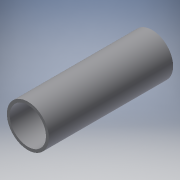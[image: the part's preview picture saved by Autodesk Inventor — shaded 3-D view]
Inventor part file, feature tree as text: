
AUTODESK INVENTOR PART (.ipt)
format: ipt  version: 2019 (Build 230136000, 136)  size: 102,400 bytes
history: native  units: mm
features: extrude x2, sketch x2
ambient origin geometry x8: Origin, YZ Plane, XZ Plane, XY Plane, X Axis, Y Axis, Z Axis, Center Point
bodies: Solid1 (feature_tree)
feature tree (4):
  extrude  "Extrusion1"  Depth=1200.0mm TaperAngle=0.0deg
  extrude  "Extrusion2"  Depth=120.0mm TaperAngle=0.0deg
  sketch  "Sketch1"  dims[d0=405.36mm d1=1200.0mm d2=0.0mm]
  sketch  "Sketch2"  dims[d3=350.0mm d4=120.0mm d5=0.0mm]
